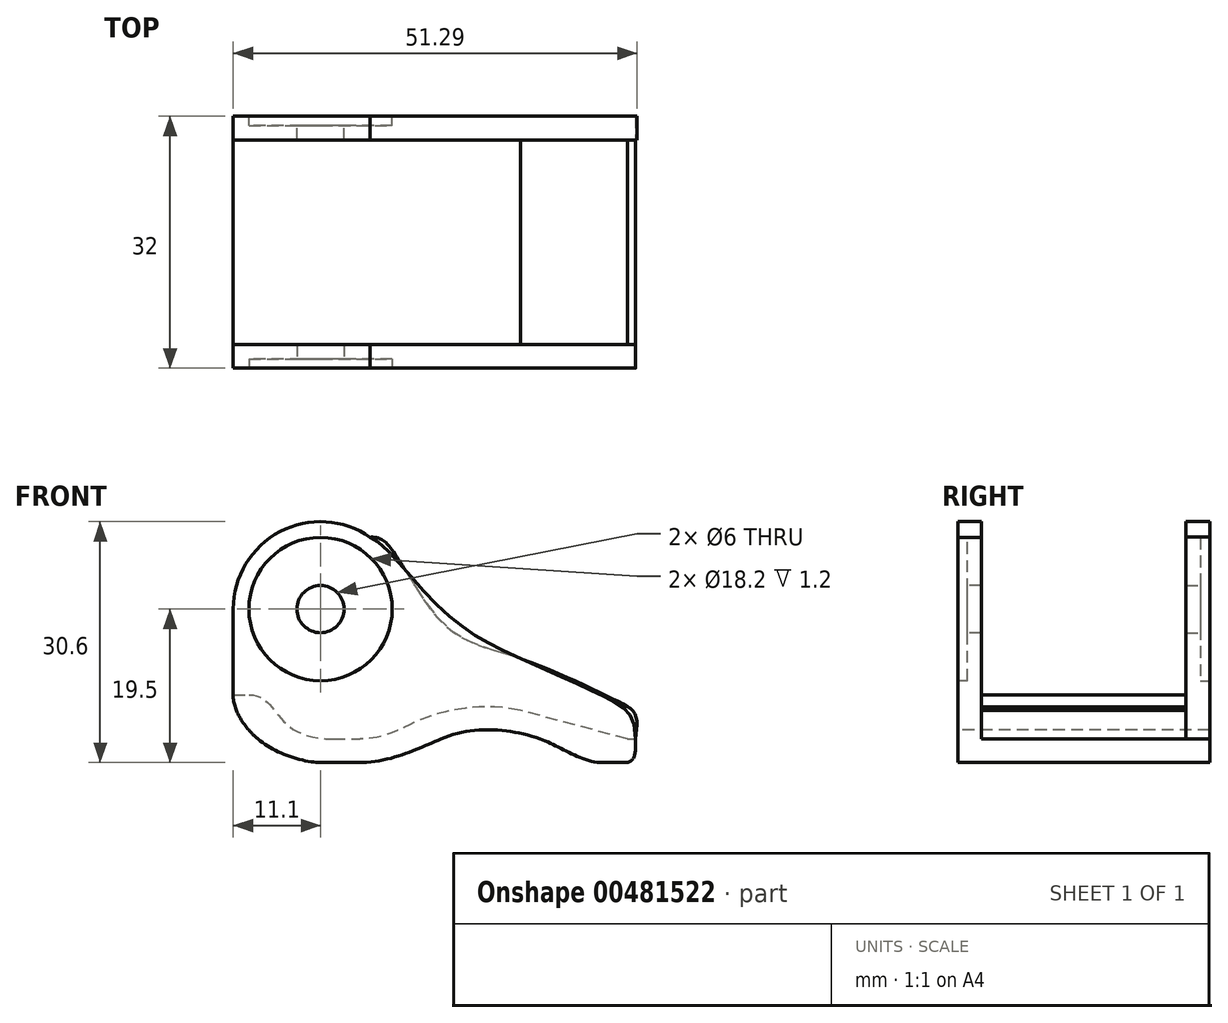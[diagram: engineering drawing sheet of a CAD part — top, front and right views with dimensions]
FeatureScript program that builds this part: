
annotation { "Feature Type Name" : "Feature", "Feature Type Description" : "" }
export const myFeature = defineFeature(function(context is Context, id is Id, definition is map)
    precondition{}
    {
        {
            var Q0;
            Q0=qCreatedBy(makeId("Front.planeOp"),FACE);
            var sketch = newSketch(context, id + "F0", { "sketchPlane" : qUnion([Q0])});
            skLineSegment(sketch, "E0.top", {"start": v(0, 3) * mm, "end": v(51.1, 3) * mm});
            skCircle(sketch, "E1", {"center": v(11.1, 19.5) * mm, "radius": 3 * mm});
            skCircle(sketch, "E2", {"center": v(11.1, 19.5) * mm, "radius": 9.1 * mm});
            skLineSegment(sketch, "E3", {"start": v(0, 3) * mm, "end": v(0, 19.5) * mm});
            skPoint(sketch, "E4.visualSharp", {"position": v(22.2, 19.5) * mm});
            skLineSegment(sketch, "E5", {"start": v(0, 8.6) * mm, "end": v(2, 8.6) * mm});
            skLineSegment(sketch, "E6", {"start": v(2, 8.6) * mm, "end": v(2, 3) * mm});
            skCircle(sketch, "E7", {"center": v(11.1, 19.5) * mm, "radius": 11.1 * mm});
            skFitSpline(sketch, "E8", {"points": [v(17.41, 28.63) * mm, v(26.4, 19.56) * mm, v(36.99, 13.03) * mm, v(48.27, 7.78) * mm, v(51.1, 3) * mm], "startDerivative": vector(20.76, -6.7) * mm, "endDerivative": vector(0, -50.66) * mm});
            skLineSegment(sketch, "E9", {"start": v(50.1, 3) * mm, "end": v(36.49, 6.65) * mm});
            skFitSpline(sketch, "E10", {"points": [v(2, 8.6) * mm, v(12.74, 3) * mm], "startDerivative": vector(12.3, 0) * mm, "endDerivative": vector(23.94, 0) * mm});
            skFitSpline(sketch, "E11", {"points": [v(36.49, 6.65) * mm, v(28.32, 6.74) * mm, v(23.03, 5.1) * mm, v(16.13, 3) * mm], "startDerivative": vector(-26.83, 5.22) * mm, "endDerivative": vector(-27.22, 0) * mm});
            skPoint(sketch, "E12", {"position": v(1, 8.6) * mm});
            skLineSegment(sketch, "E13", {"start": v(47, 0) * mm, "end": v(49.76, 0) * mm});
            skLineSegment(sketch, "E14", {"start": v(11.16, 0) * mm, "end": v(15.89, 0) * mm});
            skFitSpline(sketch, "E15", {"points": [v(51.1, 3) * mm, v(49.76, 0) * mm], "startDerivative": vector(0, -3.52) * mm, "endDerivative": vector(-4.69, 0) * mm});
            skFitSpline(sketch, "E16", {"points": [v(47, 0) * mm, v(40.44, 2.4) * mm, v(34.96, 3.99) * mm, v(29.05, 3.85) * mm, v(23.68, 1.84) * mm, v(15.89, 0) * mm], "startDerivative": vector(-34.02, 0) * mm, "endDerivative": vector(-39.84, 0) * mm});
            skFitSpline(sketch, "E17", {"points": [v(11.16, 0) * mm, v(5.5, 1.49) * mm, v(1.4, 4.87) * mm, v(0, 8.6) * mm], "startDerivative": vector(-12.2, 0) * mm, "endDerivative": vector(0, 13.08) * mm});
            skSolve(sketch);
        }
        {
            var Q0;
            {var subQ4=sQuery(id+"F0.wireOp",EDGE,"E5");Q0=makeQuery(id+"F0.imprint","IMPRINT",FACE,{"disambiguationData":[TD([[makeQuery(id+"F0.imprint","IMPRINT",EDGE,{"derivedFrom":subQ4}),-1.0]])]});}
            var Q1;
            {var subQ3=sQuery(id+"F0.wireOp",EDGE,"E5");Q1=makeQuery(id+"F0.imprint","IMPRINT",FACE,{"disambiguationData":[TD([[makeQuery(id+"F0.imprint","IMPRINT",EDGE,{"derivedFrom":subQ3}),1.0]])]});}
            var Q2;
            Q2=makeQuery(id+"F0.imprint","IMPRINT",FACE,{"disambiguationData":[TD([[makeQuery(id+"F0.imprint","IMPRINT",EDGE,{"derivedFrom":sQuery(id+"F0.wireOp",EDGE,"E1")}),-1.0]])]});
            var Q3;
            Q3=makeQuery(id+"F0.imprint","IMPRINT",FACE,{"disambiguationData":[TD([[makeQuery(id+"F0.imprint","IMPRINT",EDGE,{"derivedFrom":sQuery(id+"F0.wireOp",EDGE,"E2")}),-1.0]])]});
            var Q4;
            {var subQ0=sQuery(id+"F0.wireOp",EDGE,"E9");Q4=makeQuery(id+"F0.imprint","IMPRINT",FACE,{"disambiguationData":[TD([[makeQuery(id+"F0.imprint","IMPRINT",EDGE,{"derivedFrom":subQ0}),1.0]])]});}
            var Q5;
            {var subQ0=sQuery(id+"F0.wireOp",EDGE,"E13");Q5=makeQuery(id+"F0.imprint","IMPRINT",FACE,{"disambiguationData":[TD([[makeQuery(id+"F0.imprint","IMPRINT",EDGE,{"derivedFrom":subQ0}),1.0]])]});}
            var Q6;
            {var subQ5=sQuery(id+"F0.wireOp",EDGE,"E14");Q6=makeQuery(id+"F0.imprint","IMPRINT",FACE,{"disambiguationData":[TD([[makeQuery(id+"F0.imprint","IMPRINT",EDGE,{"derivedFrom":subQ5}),1.0]])]});}
            var Q7;
            {var subQ0=sQuery(id+"F0.wireOp",EDGE,"E10");Q7=makeQuery(id+"F0.imprint","IMPRINT",FACE,{"disambiguationData":[TD([[makeQuery(id+"F0.imprint","IMPRINT",EDGE,{"derivedFrom":subQ0}),-1.0]])]});}
            extrude(context, id + "F1", {"entities" : qUnion([Q0, Q1, Q2, Q3, Q4, Q5, Q6, Q7]), "oppositeDirection" : true, "depth" : 3 * mm, "offsetDistance" : 25 * mm});
        }
        {
            var Q0;
            {var subQ5=sQuery(id+"F0.wireOp",EDGE,"E14");Q0=makeQuery(id+"F0.imprint","IMPRINT",FACE,{"disambiguationData":[TD([[makeQuery(id+"F0.imprint","IMPRINT",EDGE,{"derivedFrom":subQ5}),1.0]])]});}
            var Q1;
            {var subQ4=sQuery(id+"F0.wireOp",EDGE,"E5");Q1=makeQuery(id+"F0.imprint","IMPRINT",FACE,{"disambiguationData":[TD([[makeQuery(id+"F0.imprint","IMPRINT",EDGE,{"derivedFrom":subQ4}),-1.0]])]});}
            var Q2;
            {var subQ0=sQuery(id+"F0.wireOp",EDGE,"E9");Q2=makeQuery(id+"F0.imprint","IMPRINT",FACE,{"disambiguationData":[TD([[makeQuery(id+"F0.imprint","IMPRINT",EDGE,{"derivedFrom":subQ0}),1.0]])]});}
            var Q3;
            {var subQ0=sQuery(id+"F0.wireOp",EDGE,"E13");Q3=makeQuery(id+"F0.imprint","IMPRINT",FACE,{"disambiguationData":[TD([[makeQuery(id+"F0.imprint","IMPRINT",EDGE,{"derivedFrom":subQ0}),1.0]])]});}
            var Q4;
            {var subQ0=sQuery(id+"F0.wireOp",EDGE,"E10");Q4=makeQuery(id+"F0.imprint","IMPRINT",FACE,{"disambiguationData":[TD([[makeQuery(id+"F0.imprint","IMPRINT",EDGE,{"derivedFrom":subQ0}),-1.0]])]});}
            extrude(context, id + "F2", {"entities" : qUnion([Q0, Q1, Q2, Q3, Q4]), "operationType" : NewBodyOperationType.ADD, "oppositeDirection" : true, "depth" : 32 * mm, "offsetDistance" : 25 * mm});
        }
        {
            var Q0;
            Q0=makeQuery(id+"F2.opExtrude","CAP_FACE",FACE,{"disambiguationData":[OSD([sQuery(id+"F0.wireOp",EDGE,"E0.bottom"),sQuery(id+"F0.wireOp",EDGE,"E0.top"),sQuery(id+"F0.wireOp",EDGE,"E0.left"),sQuery(id+"F0.wireOp",EDGE,"E0.right"),sQuery(id+"F0.wireOp",EDGE,"E3"),sQuery(id+"F0.wireOp",EDGE,"E5"),sQuery(id+"F0.wireOp",EDGE,"E6")])],"isStart":false});
            var sketch = newSketch(context, id + "F3", { "sketchPlane" : qUnion([Q0])});
            skFitSpline(sketch, "E18.0", {"points": [v(-17.41, 28.63) * mm, v(-19.32, 28.01) * mm, v(-26.51, 17.8) * mm, v(-36.3, 13.29) * mm, v(-48.62, 7.9) * mm, v(-51.1, 6.06) * mm, v(-51.1, 3) * mm]});
            skArc(sketch, "E18.1", {"start": v(-17.41, 28.63) * mm, "mid": v(-5.95, 29.33) * mm, "end": v(0, 19.5) * mm});
            skLineSegment(sketch, "E18.2", {"start": v(0, 8.6) * mm, "end": v(0, 19.5) * mm});
            skCircle(sketch, "E18.3", {"center": v(-11.1, 19.5) * mm, "radius": 3 * mm});
            skFitSpline(sketch, "E18.4", {"points": [v(-47, 0) * mm, v(-44.63, 0) * mm, v(-40.52, 2.73) * mm, v(-35.1, 4.22) * mm, v(-28.85, 4.28) * mm, v(-23.64, 1.66) * mm, v(-18.85, 0) * mm, v(-15.89, 0) * mm]});
            skLineSegment(sketch, "E18.5", {"start": v(-11.16, 0) * mm, "end": v(-15.89, 0) * mm});
            skFitSpline(sketch, "E18.6", {"points": [v(-7.34, 0) * mm, v(-6.07, 0) * mm, v(-3.49, 1.03) * mm, v(-0.64, 4.16) * mm, v(0, 5.7) * mm, v(0, 8.6) * mm]});
            skLineSegment(sketch, "E18.7", {"start": v(-47, 0) * mm, "end": v(-49.76, 0) * mm});
            skFitSpline(sketch, "E18.8", {"points": [v(-51.1, 3) * mm, v(-51.1, 1.83) * mm, v(-51.33, 0) * mm, v(-49.76, 0) * mm]});
            skCircle(sketch, "E19.0", {"center": v(-11.1, 19.5) * mm, "radius": 9.1 * mm});
            skSolve(sketch);
        }
        {
            var Q0;
            Q0=makeQuery(id+"F3.imprint","IMPRINT",FACE,{"disambiguationData":[TD([[makeQuery(id+"F3.imprint","IMPRINT",EDGE,{"derivedFrom":sQuery(id+"F3.wireOp",EDGE,"E18.0")}),1.0]])]});
            var Q1;
            Q1=makeQuery(id+"F3.imprint","IMPRINT",FACE,{"disambiguationData":[TD([[makeQuery(id+"F3.imprint","IMPRINT",EDGE,{"derivedFrom":sQuery(id+"F3.wireOp",EDGE,"E18.3")}),-1.0]])]});
            extrude(context, id + "F4", {"entities" : qUnion([Q0, Q1]), "operationType" : NewBodyOperationType.ADD, "oppositeDirection" : true, "depth" : 3 * mm, "offsetDistance" : 25 * mm});
        }
        {
            var Q0;
            Q0=makeQuery(id+"F0.imprint","IMPRINT",FACE,{"disambiguationData":[TD([[makeQuery(id+"F0.imprint","IMPRINT",EDGE,{"derivedFrom":sQuery(id+"F0.wireOp",EDGE,"E1")}),-1.0]])]});
            extrude(context, id + "F5", {"entities" : qUnion([Q0]), "operationType" : NewBodyOperationType.REMOVE, "oppositeDirection" : true, "depth" : 1.2 * mm, "offsetDistance" : 25 * mm});
        }
        {
            var Q0;
            Q0=makeQuery(id+"F3.imprint","IMPRINT",FACE,{"disambiguationData":[TD([[makeQuery(id+"F3.imprint","IMPRINT",EDGE,{"derivedFrom":sQuery(id+"F3.wireOp",EDGE,"E18.3")}),-1.0]])]});
            extrude(context, id + "F6", {"entities" : qUnion([Q0]), "operationType" : NewBodyOperationType.REMOVE, "oppositeDirection" : true, "depth" : 1.2 * mm, "offsetDistance" : 25 * mm});
        }
    });
